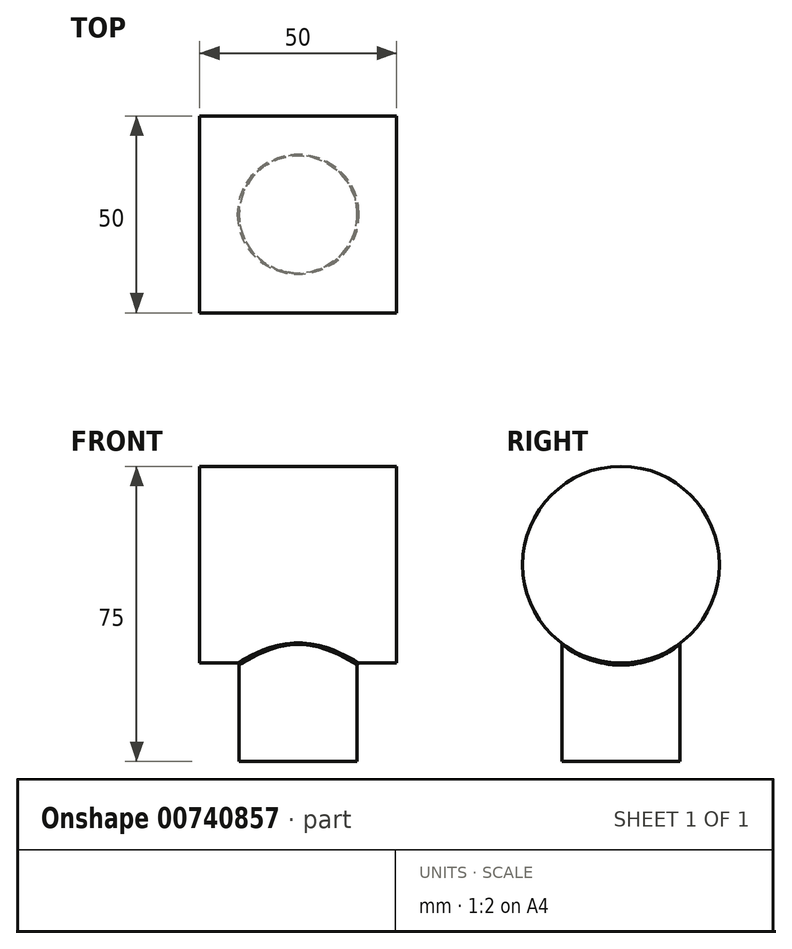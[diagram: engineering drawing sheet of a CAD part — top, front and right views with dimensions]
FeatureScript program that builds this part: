
annotation { "Feature Type Name" : "Feature", "Feature Type Description" : "" }
export const myFeature = defineFeature(function(context is Context, id is Id, definition is map)
    precondition{}
    {
        {
            var Q0;
            Q0=qCreatedBy(makeId("Right.planeOp"),FACE);
            var sketch = newSketch(context, id + "F0", { "sketchPlane" : qUnion([Q0])});
            skCircle(sketch, "E0", {"center": v(0, 0) * mm, "radius": 25 * mm});
            skSolve(sketch);
        }
        {
            var Q0;
            Q0 = qSketchRegion(id + "F0", true);
            extrude(context, id + "F1", {"entities" : qUnion([Q0]), "endBound" : BoundingType.SYMMETRIC, "depth" : 50 * mm, "offsetDistance" : 25 * mm});
        }
        {
            var Q0;
            Q0=qCreatedBy(makeId("Top.planeOp"),FACE);
            var sketch = newSketch(context, id + "F2", { "sketchPlane" : qUnion([Q0])});
            skCircle(sketch, "E1", {"center": v(0, 0) * mm, "radius": 15 * mm});
            skSolve(sketch);
        }
        {
            var Q0;
            Q0 = qSketchRegion(id + "F2", true);
            extrude(context, id + "F3", {"entities" : qUnion([Q0]), "operationType" : NewBodyOperationType.ADD, "oppositeDirection" : true, "depth" : 50 * mm, "offsetDistance" : 25 * mm});
        }
        {
            var Q0;
            Q0=makeQuery(id+"F3.boolean.opBoolean","INTERSECT",EDGE,{"derivedFrom":[makeQuery(id+"F1.opExtrude","SWEPT_FACE",FACE,{"disambiguationData":[OSD([sQuery(id+"F0.wireOp",EDGE,"E0")])]}),makeQuery(id+"F3.opExtrude","SWEPT_FACE",FACE,{"disambiguationData":[OSD([sQuery(id+"F2.wireOp",EDGE,"E1")])]})]});
            fillet(context, id + "F4", {"entities" : qUnion([Q0]), "radius" : 0.5 * mm, "tangentPropagation" : true, "allowEdgeOverflow" : false});
        }
    });
